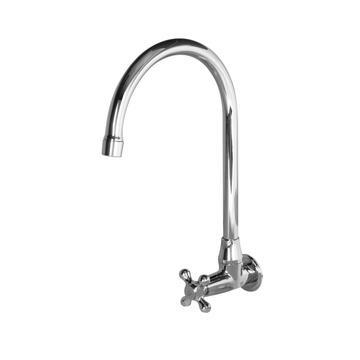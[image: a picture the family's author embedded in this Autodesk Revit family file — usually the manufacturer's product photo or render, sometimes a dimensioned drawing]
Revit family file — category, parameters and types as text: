
# Revit family: 01-0834-11-LLAVE MÓVIL PARED ARCO CALIMA
name_source: partatom
category: Plumbing Fixtures
revit_build: Autodesk Revit 2018 (Build: 20170223_1515(x64)
units: mm (PartAtom-declared; Revit-internal decimal feet)

## family parameters
Cut with Voids When Loaded = No
Host = Face
OmniClass Number = 23.31.11.00
Part Type = Normal
Room Calculation Point = No
Round Connector Dimension = Use Diameter
Shared = No

## types (1)
- 01-0834-11
    Alto = 330 mm
    Alto cuerpo-llave = 110 mm  [stored 0.360892 ft]
    Ancho  manija = 69 mm  [stored 0.226378 ft]
    CW Connection = Yes
    Default Elevation = 0 mm  [stored 0 ft]
    Description = Monomando
    HW Connection = Yes
    Link Ficha Tecnica = http://infotecnica.gricol.com
    Manufacturer = Gricol
    Model = 01-0834-11
    Plástico - ABS Cromado = Plastico ABS Cromado
    Product Name = LLAVE MÓVIL PARED ARCO CALIMA
    Profundidad = 187 mm  [stored 0.613517 ft]
    Type Image = 01-0834-11-FOTO LLAVE MOVIL ARCO CALIMA.jpg
    URL = https://www.gricol.com
    Vent Connection = No
    Waste Connection = No

note: [stored X ft] marks values corroborated as IEEE doubles in the binary element streams (Revit-internal decimal feet)

## geometry (parser evidence)
native form markers: Blend x2, Sweep x8
no freeform markers — native parametric forms only
